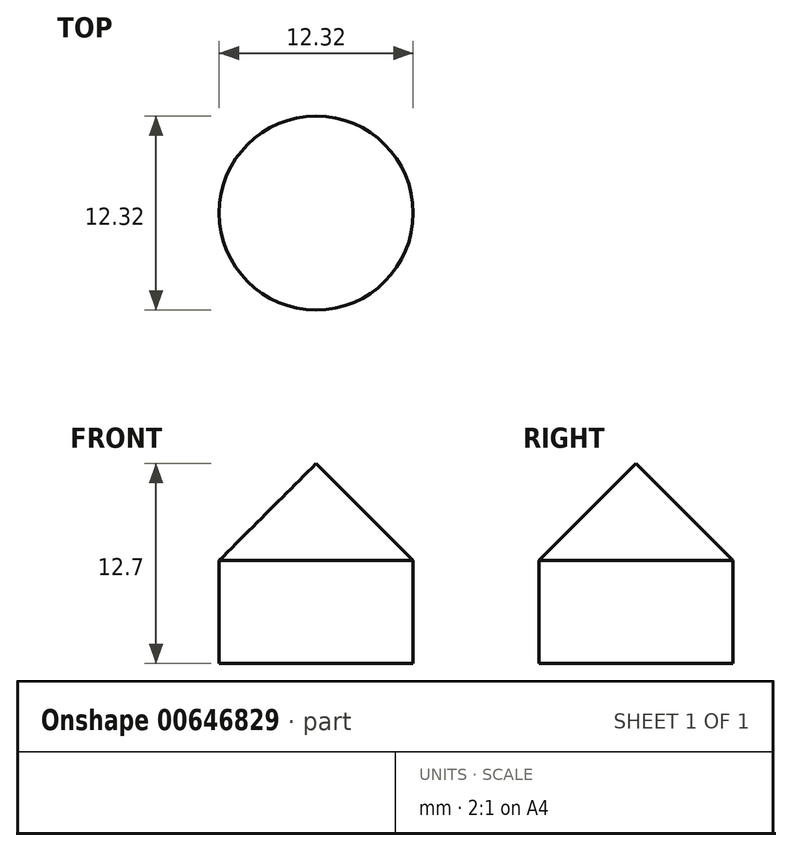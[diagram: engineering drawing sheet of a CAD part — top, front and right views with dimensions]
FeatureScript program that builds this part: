
annotation { "Feature Type Name" : "Feature", "Feature Type Description" : "" }
export const myFeature = defineFeature(function(context is Context, id is Id, definition is map)
    precondition{}
    {
        {
            var Q0;
            Q0=qCreatedBy(makeId("Top.planeOp"),FACE);
            var sketch = newSketch(context, id + "F0", { "sketchPlane" : qUnion([Q0])});
            skCircle(sketch, "E0", {"center": v(0, 0) * mm, "radius": 6.16 * mm});
            skSolve(sketch);
        }
        {
            var Q0;
            Q0=makeQuery(id+"F0.imprint","IMPRINT",FACE,{"disambiguationData":[TD([[makeQuery(id+"F0.imprint","IMPRINT",EDGE,{"derivedFrom":sQuery(id+"F0.wireOp",EDGE,"E0")}),1.0]])]});
            extrude(context, id + "F1", {"entities" : qUnion([Q0]), "depth" : 12.7 * mm, "offsetDistance" : 25.4 * mm});
        }
        {
            var Q0;
            Q0=makeQuery(id+"F1.opExtrude","CAP_FACE",FACE,{"disambiguationData":[OSD([sQuery(id+"F0.wireOp",EDGE,"E0")])],"isStart":false});
            chamfer(context, id + "F2", {"entities" : qUnion([Q0]), "width" : 6.16 * mm, "tangentPropagation" : true});
        }
    });
